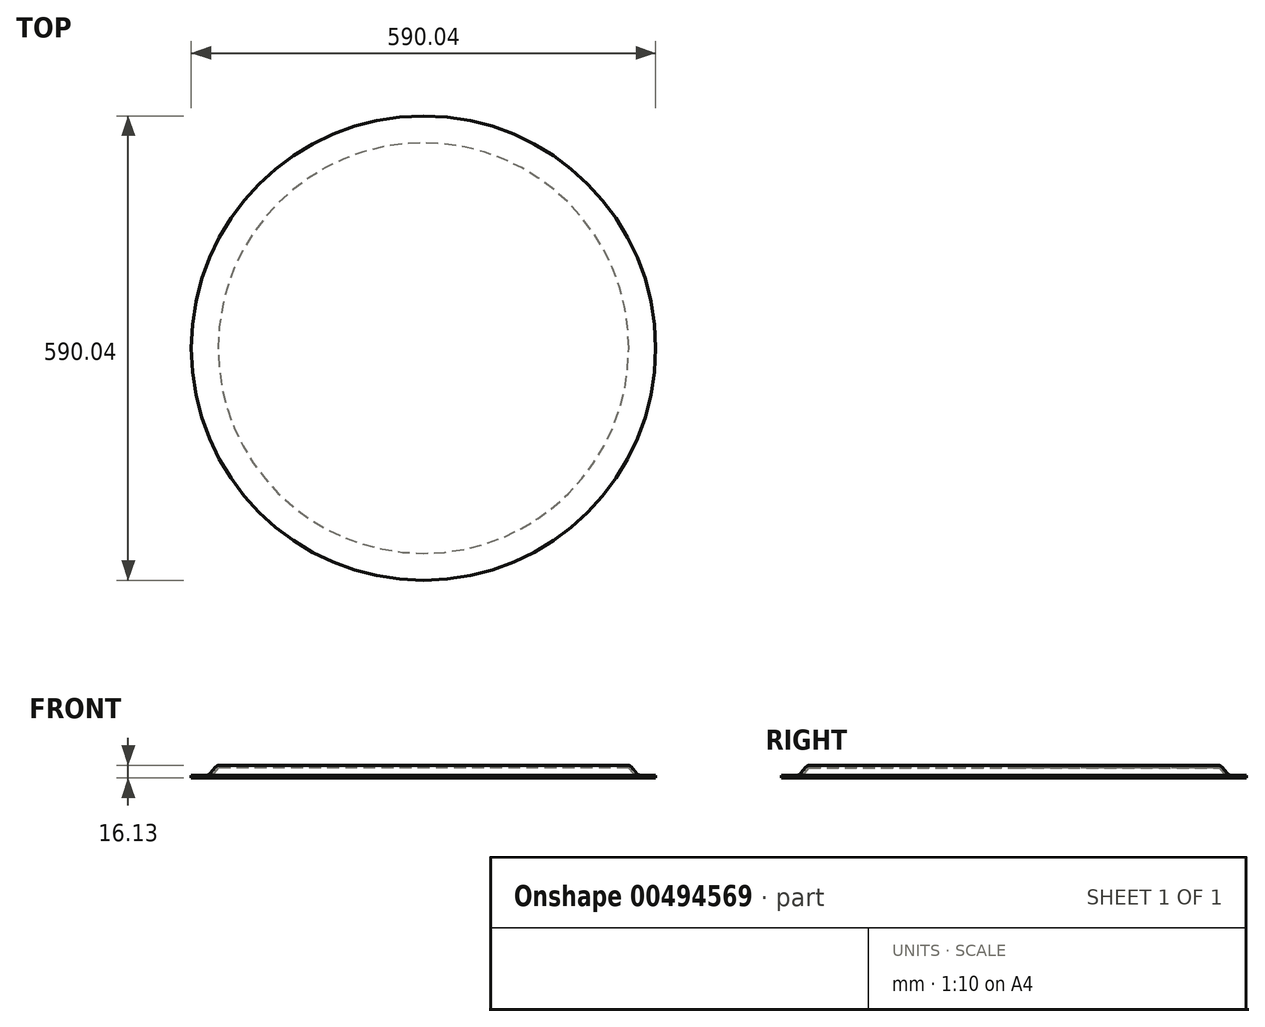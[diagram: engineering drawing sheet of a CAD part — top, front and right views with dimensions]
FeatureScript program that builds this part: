
annotation { "Feature Type Name" : "Feature", "Feature Type Description" : "" }
export const myFeature = defineFeature(function(context is Context, id is Id, definition is map)
    precondition{}
    {
        {
            var Q0;
            Q0=qCreatedBy(makeId("Front.planeOp"),FACE);
            var sketch = newSketch(context, id + "F0", { "sketchPlane" : qUnion([Q0])});
            skLineSegment(sketch, "E0", {"start": v(0, 0) * mm, "end": v(259.4, 0) * mm});
            skLineSegment(sketch, "E1", {"start": v(275.97, -12.7) * mm, "end": v(295.02, -12.7) * mm});
            skLineSegment(sketch, "E2", {"start": v(271.1, -10.43) * mm, "end": v(264.26, -2.27) * mm});
            skPoint(sketch, "E3.visualSharp", {"position": v(262.36, 0) * mm});
            skArc(sketch, "E3.filletArc", {"start": v(264.26, -2.27) * mm, "mid": v(262.08, -0.6) * mm, "end": v(259.4, 0) * mm});
            skPoint(sketch, "E4.visualSharp", {"position": v(273, -12.7) * mm});
            skArc(sketch, "E4.filletArc", {"start": v(271.1, -10.43) * mm, "mid": v(273.29, -12.1) * mm, "end": v(275.97, -12.7) * mm});
            skLineSegment(sketch, "E5.0", {"start": v(275.97, -16.13) * mm, "end": v(295.02, -16.13) * mm});
            skArc(sketch, "E5.1", {"start": v(268.48, -12.63) * mm, "mid": v(271.84, -15.21) * mm, "end": v(275.97, -16.13) * mm});
            skLineSegment(sketch, "E5.2", {"start": v(268.48, -12.63) * mm, "end": v(260.76, -3.43) * mm});
            skLineSegment(sketch, "E5.3", {"start": v(0, -3.43) * mm, "end": v(260.76, -3.43) * mm});
            skLineSegment(sketch, "E6", {"start": v(0, 0) * mm, "end": v(0, -3.43) * mm});
            skLineSegment(sketch, "E7", {"start": v(295.02, -12.7) * mm, "end": v(295.02, -16.13) * mm});
            skSolve(sketch);
        }
        {
            var Q0;
            Q0=makeQuery(id+"F0.imprint","IMPRINT",FACE,{"disambiguationData":[TD([[makeQuery(id+"F0.imprint","IMPRINT",EDGE,{"derivedFrom":sQuery(id+"F0.wireOp",EDGE,"E0")}),-1.0]])]});
            var Q1;
            Q1=sQuery(id+"F0.wireOp",EDGE,"E6");
            revolve(context, id + "F1", {"entities" : qUnion([Q0]), "axis" : qUnion([Q1]), "revolveType" : RevolveType.FULL});
        }
    });
